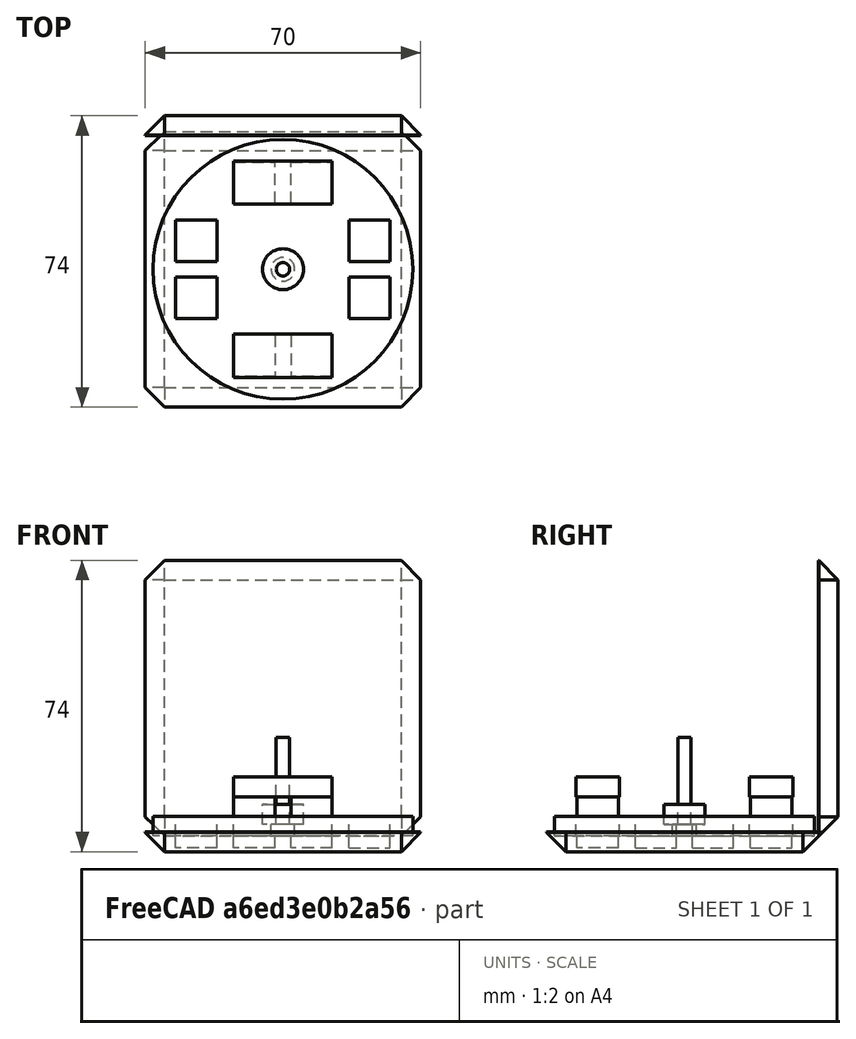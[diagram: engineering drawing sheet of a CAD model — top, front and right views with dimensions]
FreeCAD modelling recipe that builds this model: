
FCSTD DOCUMENT  (FreeCAD 0.18.4R)
Label: magnet-clamp
License: All rights reserved
LicenseURL: http://en.wikipedia.org/wiki/All_rights_reserved
objects: Part::Feature×13, Part::Box×9, Part::Cylinder×4, Part::MultiFuse×4, Part::Chamfer×2, Part::Fuse×1, Part::Mirroring×1
note: 34 computed .brp shape members not serialized (recipe doc carries the construction recipe); baked Part::Feature solids carry a one-line shape summary decoded from their .brp

FEATURE [Part::Box] Box  label="Long Magnet"
  AttacherType = Attacher::AttachEngine3D
  Height = 5
  Length = 25
  Placement = pos=(-12.5,16.5,0) rot=(0,0,1;0rad)
  Width = 11
FEATURE [Part::Cylinder] Cylinder001
  Angle = 360
  AttacherType = Attacher::AttachEngine3D
  Height = 25
  Radius = 1.7
FEATURE [Part::Cylinder] Cylinder002
  Angle = 360
  AttacherType = Attacher::AttachEngine3D
  Height = 3
  Radius = 3
FEATURE [Part::Fuse] Fusion  label="Screw"
  Base = -> Cylinder001
  Tool = -> Cylinder002
FEATURE [Part::Box] Box004  label="Square Magnet"
  AttacherType = Attacher::AttachEngine3D
  Height = 5
  Length = 10.5
  Placement = pos=(2,16.75,5) rot=(0,0,1;0rad)
  Width = 10.5
FEATURE [Part::Cylinder] Cylinder004  label="bearing001"
  Angle = 360
  AttacherType = Attacher::AttachEngine3D
  Height = 5
  Placement = pos=(0,0,3) rot=(0,0,1;0rad)
  Radius = 5.2
FEATURE [Part::Box] Box005  label="Square Magnet001"
  AttacherType = Attacher::AttachEngine3D
  Height = 5
  Length = 10.5
  Placement = pos=(-12.5,16.75,5) rot=(0,0,1;0rad)
  Width = 10.5
FEATURE [Part::Cylinder] Cylinder  label="rotating-disc"
  Angle = 360
  AttacherType = Attacher::AttachEngine3D
  Height = 5
  Radius = 33
FEATURE [Part::Box] Box006  label="Square Magnet002"
  AttacherType = Attacher::AttachEngine3D
  Height = 3
  Length = 10.5
  Placement = pos=(2,16.75,-3) rot=(0,0,1;0rad)
  Width = 10.5
FEATURE [Part::Box] Box007  label="Square Magnet003"
  AttacherType = Attacher::AttachEngine3D
  Height = 3
  Length = 10.5
  Placement = pos=(-12.5,16.75,-3) rot=(0,0,1;0rad)
  Width = 10.5
FEATURE [Part::Feature] Box011
  Placement = pos=(12.5,-16.5,0) rot=(0,0,1;3.14159rad)
  shape: bbox 25 x 11 x 5 mm, 6 faces (baked)
FEATURE [Part::Feature] Box004002
  Placement = pos=(-2,-16.75,5) rot=(0,0,1;3.14159rad)
  shape: bbox 10.5 x 10.5 x 5 mm, 6 faces (baked)
FEATURE [Part::Feature] Box005002
  Placement = pos=(12.5,-16.75,5) rot=(0,0,1;3.14159rad)
  shape: bbox 10.5 x 10.5 x 5 mm, 6 faces (baked)
FEATURE [Part::Feature] Box006001
  Placement = pos=(-16.75,2,-3) rot=(0,0,1;1.5708rad)
  shape: bbox 10.5 x 10.5 x 3 mm, 6 faces (baked)
FEATURE [Part::Feature] Box006002
  Placement = pos=(-2,-16.75,-3) rot=(0,0,1;3.14159rad)
  shape: bbox 10.5 x 10.5 x 3 mm, 6 faces (baked)
FEATURE [Part::Feature] Box006003
  Placement = pos=(16.75,-2,-3) rot=(0,0,-1;1.5708rad)
  shape: bbox 10.5 x 10.5 x 3 mm, 6 faces (baked)
FEATURE [Part::Feature] Box007001
  Placement = pos=(-16.75,-12.5,-3) rot=(0,0,1;1.5708rad)
  shape: bbox 10.5 x 10.5 x 3 mm, 6 faces (baked)
FEATURE [Part::Feature] Box007002
  Placement = pos=(12.5,-16.75,-3) rot=(0,0,1;3.14159rad)
  shape: bbox 10.5 x 10.5 x 3 mm, 6 faces (baked)
FEATURE [Part::Feature] Box007003
  Placement = pos=(16.75,12.5,-3) rot=(0,0,-1;1.5708rad)
  shape: bbox 10.5 x 10.5 x 3 mm, 6 faces (baked)
FEATURE [Part::Feature] Box008001
  Placement = pos=(-16.75,2,0) rot=(0,0,1;1.5708rad)
  shape: bbox 10.5 x 10.5 x 5 mm, 6 faces (baked)
FEATURE [Part::Feature] Box008003
  Placement = pos=(16.75,-2,0) rot=(0,0,-1;1.5708rad)
  shape: bbox 10.5 x 10.5 x 5 mm, 6 faces (baked)
FEATURE [Part::Feature] Box009001
  Placement = pos=(-16.75,-12.5,0) rot=(0,0,1;1.5708rad)
  shape: bbox 10.5 x 10.5 x 5 mm, 6 faces (baked)
FEATURE [Part::Feature] Box009003
  Placement = pos=(16.75,12.5,0) rot=(0,0,-1;1.5708rad)
  shape: bbox 10.5 x 10.5 x 5 mm, 6 faces (baked)
FEATURE [Part::MultiFuse] Fusion001  label="keeper-holes"
  Shapes = -> [Box009001,Box009003,Box008003,Box008001,Box,Box011]
FEATURE [Part::MultiFuse] Fusion002  label="magnets"
  Shapes = -> [Box004,Box005,Box004002,Box005002]
FEATURE [Part::MultiFuse] Fusion003  label="conductors"
  Shapes = -> [Box006001,Box007002,Box007001,Box007003,Box006002,Box006003,Box006,Box007]
FEATURE [Part::Box] Box009004  label="Long Magnet001"
  AttacherType = Attacher::AttachEngine3D
  Height = 5
  Length = 25
  Placement = pos=(-12.5,16.5,10) rot=(0,0,1;0rad)
  Width = 11
FEATURE [Part::Box] Box009005  label="Long Magnet002"
  AttacherType = Attacher::AttachEngine3D
  Height = 5
  Length = 25
  Placement = pos=(-12.5,16.5,10) rot=(0,0,1;0rad)
  Width = 11
FEATURE [Part::Mirroring] Part__Mirroring  label="Long Magnet002 (Mirror #1)"
  Base = (0,0,0)
  Normal = (0,1,0)
  Source = -> Box009005
FEATURE [Part::MultiFuse] Fusion004  label="stationary-keepers"
  Shapes = -> [Box009004,Part__Mirroring]
FEATURE [Part::Box] Box009006  label="Cube"
  AttacherType = Attacher::AttachEngine3D
  Height = 5
  Length = 70
  Placement = pos=(-35,-35,-4) rot=(0,0,1;0rad)
  Width = 70
FEATURE [Part::Chamfer] Chamfer  label="face"
  Base = -> Box009006
  Edges = 8 edges r=4.9: [Edge1,Edge3,Edge4,Edge5,Edge7,Edge8,Edge9,Edge11]
FEATURE [Part::Box] Box009007  label="Cube001"
  AttacherType = Attacher::AttachEngine3D
  Height = 5
  Length = 70
  Placement = pos=(-35,-35,-4) rot=(0,0,1;0rad)
  Width = 70
FEATURE [Part::Chamfer] Chamfer001  label="face001"
  Base = -> Box009007
  Edges = 8 edges r=4.9: [Edge1,Edge3,Edge4,Edge5,Edge7,Edge8,Edge9,Edge11]
  Placement = pos=(0,35,35) rot=(1,0,0;1.5708rad)
